# Revit family: NBS_COBAFlooring_EntMatt_Alba
name_source: partatom
category: Generic Models
revit_build: Autodesk Revit 2015 (Build: 20140606_1530(x64)
units: mm (PartAtom-declared; Revit-internal decimal feet)

## types (1)
- Plan A Aluminium Entrance Matting
    Arrangement = Can be internally inset in a matwell or loose laid with ramped edging
    AssetType = Fixed
    BIMObjectName = NBS_COBAFlooring_EntranceMatting_PlanAAluminiumEntranceMatting
    BaseColour = Aluminium
    BaseMaterial = 30% recycled aluminium profiles
    CarpetColourOptions = Anthracite, Blue, Brown, Charcoal, Grey
    Category = Pr_35_57_11_26:Entrance mats
    Combustible = No
    Construction = Open
    Default Elevation = 1200 mm
    Description = Versatile aluminium entrance matting
    DurationUnit = year
    EdgingMaterial = NBS_Concept
    EntranceMattingHeight = 18 mm  [stored 0.0590551 ft]
    EntranceMattingMaterial = NBS_COBAFlooring_Carpet_PlanA
    Features = Suitable for heavy-duty use
    Finish = Carpet or PVC strips in an aluminium frame
    FireRating = Cfl-s1
    HasAntiStaticSurface = Yes
    HasNonSkidSurface = No
    IfcExportAs = IfcCoveringType
    IfcExportType = FLOORING
    IntegralAccessories = P456 - Aluminium finishing profile, P457 - PVC expansion strip, P460 - T profile, P461 - Frame profile for recessed wells, P463 - Corner pieces for frame profile
    LinkingJoints = Black PVC
    ManufacturerName = COBA Flooring
    ManufacturerURL = www.cobaeurope.com
    MattingHeight = 18 mm
    ModelReference = Plan A Aluminium Entrance Matting
    NBSCertification = www.nationalbimlibrary.com/cert/2kld41dn
    NBSDescription = Entrance matting
    NBSReference = 45-35-35/420
    Name = EntranceMatting_PlanAAluminiumEntranceMatting_COBAFlooring
    NominalHeight = 18 mm  [stored 0.0590551 ft]
    Pattern = Horizontal strips
    ProductInformation = www.cobaeurope.com/entrance-matting-systems/-/datasheets/plan-a.pdf
    SurfaceInsertOptions = Atrium nylon carpet, Needlepunch PP carpet, PVC, Carpet and PVC
    SurfaceInsertWidth = 20 mm
    TotalThickness = 0 mm  [stored 0 ft]
    TrafficType = Pedestrian, wheel chairs, pushchairs and trolleys
    Uniclass2015Code = Pr_35_57_11_26
    Uniclass2015Title = Entrance mats
    Uniclass2015Version = Products v1.5
    Version = 4
    WarrantyDurationParts = 5 years
    WarrantyDurationUnit = year

note: [stored X ft] marks values corroborated as IEEE doubles in the binary element streams (Revit-internal decimal feet)

## geometry (parser evidence)
native form markers: Sweep x2
no freeform markers — native parametric forms only
